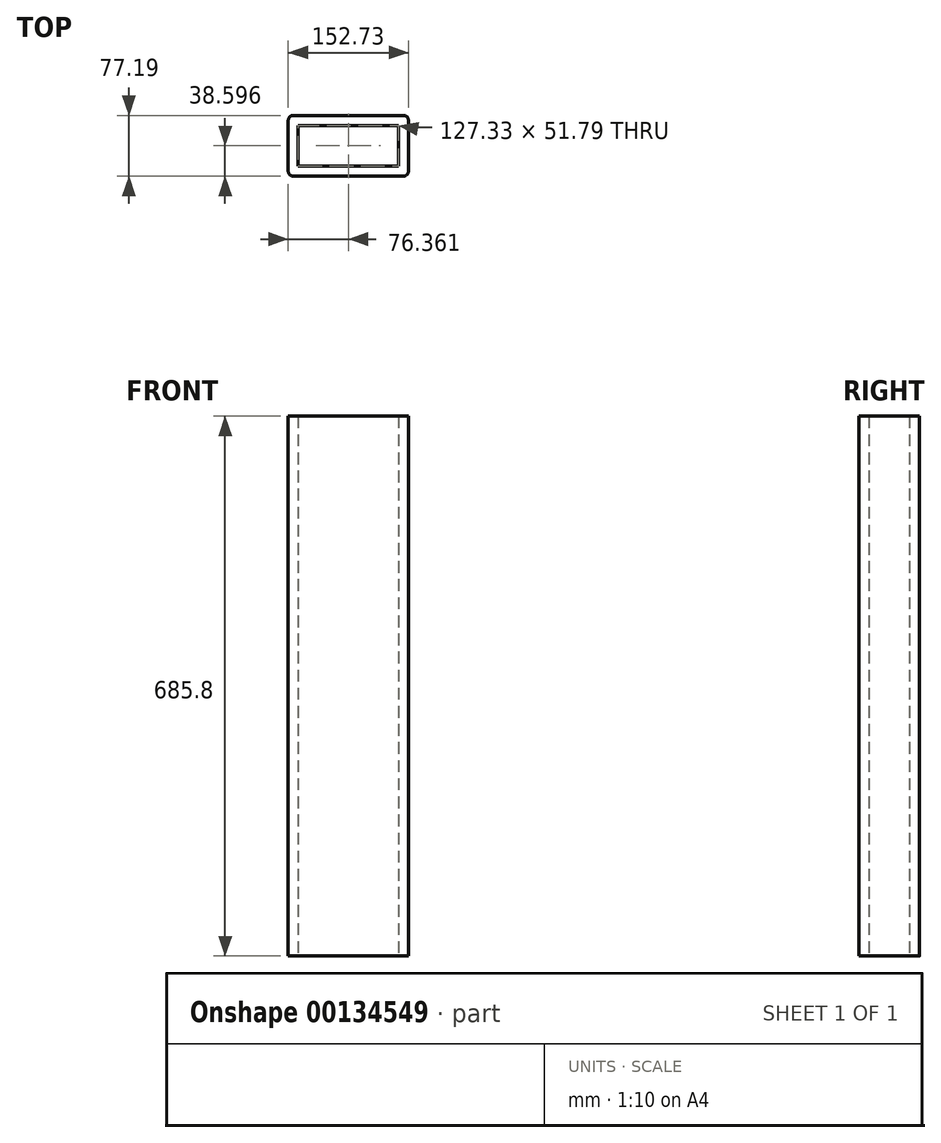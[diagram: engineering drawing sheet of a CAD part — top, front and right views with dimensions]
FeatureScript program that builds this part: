
annotation { "Feature Type Name" : "Feature", "Feature Type Description" : "" }
export const myFeature = defineFeature(function(context is Context, id is Id, definition is map)
    precondition{}
    {
        {
            var Q0;
            Q0=qCreatedBy(makeId("Top.planeOp"),FACE);
            var sketch = newSketch(context, id + "F0", { "sketchPlane" : qUnion([Q0])});
            skLineSegment(sketch, "E0.bottom", {"start": v(-23.78, 31.37) * mm, "end": v(116.25, 31.37) * mm});
            skLineSegment(sketch, "E0.top", {"start": v(-23.78, -45.82) * mm, "end": v(116.25, -45.82) * mm});
            skLineSegment(sketch, "E0.left", {"start": v(-30.13, 25.02) * mm, "end": v(-30.13, -39.47) * mm});
            skLineSegment(sketch, "E0.right", {"start": v(122.6, 25.02) * mm, "end": v(122.6, -39.47) * mm});
            skPoint(sketch, "E1.visualSharp", {"position": v(-30.13, 31.37) * mm});
            skArc(sketch, "E1.filletArc", {"start": v(-23.78, 31.37) * mm, "mid": v(-28.27, 29.51) * mm, "end": v(-30.13, 25.02) * mm});
            skPoint(sketch, "E2.visualSharp", {"position": v(-30.13, -45.82) * mm});
            skArc(sketch, "E2.filletArc", {"start": v(-30.13, -39.47) * mm, "mid": v(-28.27, -43.96) * mm, "end": v(-23.78, -45.82) * mm});
            skPoint(sketch, "E3.visualSharp", {"position": v(122.6, -45.82) * mm});
            skArc(sketch, "E3.filletArc", {"start": v(116.25, -45.82) * mm, "mid": v(120.74, -43.96) * mm, "end": v(122.6, -39.47) * mm});
            skPoint(sketch, "E4.visualSharp", {"position": v(122.6, 31.37) * mm});
            skArc(sketch, "E4.filletArc", {"start": v(122.6, 25.02) * mm, "mid": v(120.74, 29.51) * mm, "end": v(116.25, 31.37) * mm});
            skLineSegment(sketch, "E5.0", {"start": v(-17.43, 18.67) * mm, "end": v(-17.43, -33.12) * mm});
            skLineSegment(sketch, "E5.1", {"start": v(-17.43, 18.67) * mm, "end": v(109.9, 18.67) * mm});
            skLineSegment(sketch, "E5.2", {"start": v(109.9, 18.67) * mm, "end": v(109.9, -33.12) * mm});
            skLineSegment(sketch, "E5.3", {"start": v(-17.43, -33.12) * mm, "end": v(109.9, -33.12) * mm});
            skSolve(sketch);
        }
        {
            var Q0;
            Q0=makeQuery(id+"F0.imprint","IMPRINT",FACE,{"disambiguationData":[TD([[makeQuery(id+"F0.imprint","IMPRINT",EDGE,{"derivedFrom":sQuery(id+"F0.wireOp",EDGE,"E0.bottom")}),-1.0]])]});
            extrude(context, id + "F1", {"entities" : qUnion([Q0]), "depth" : 685.8 * mm});
        }
    });
